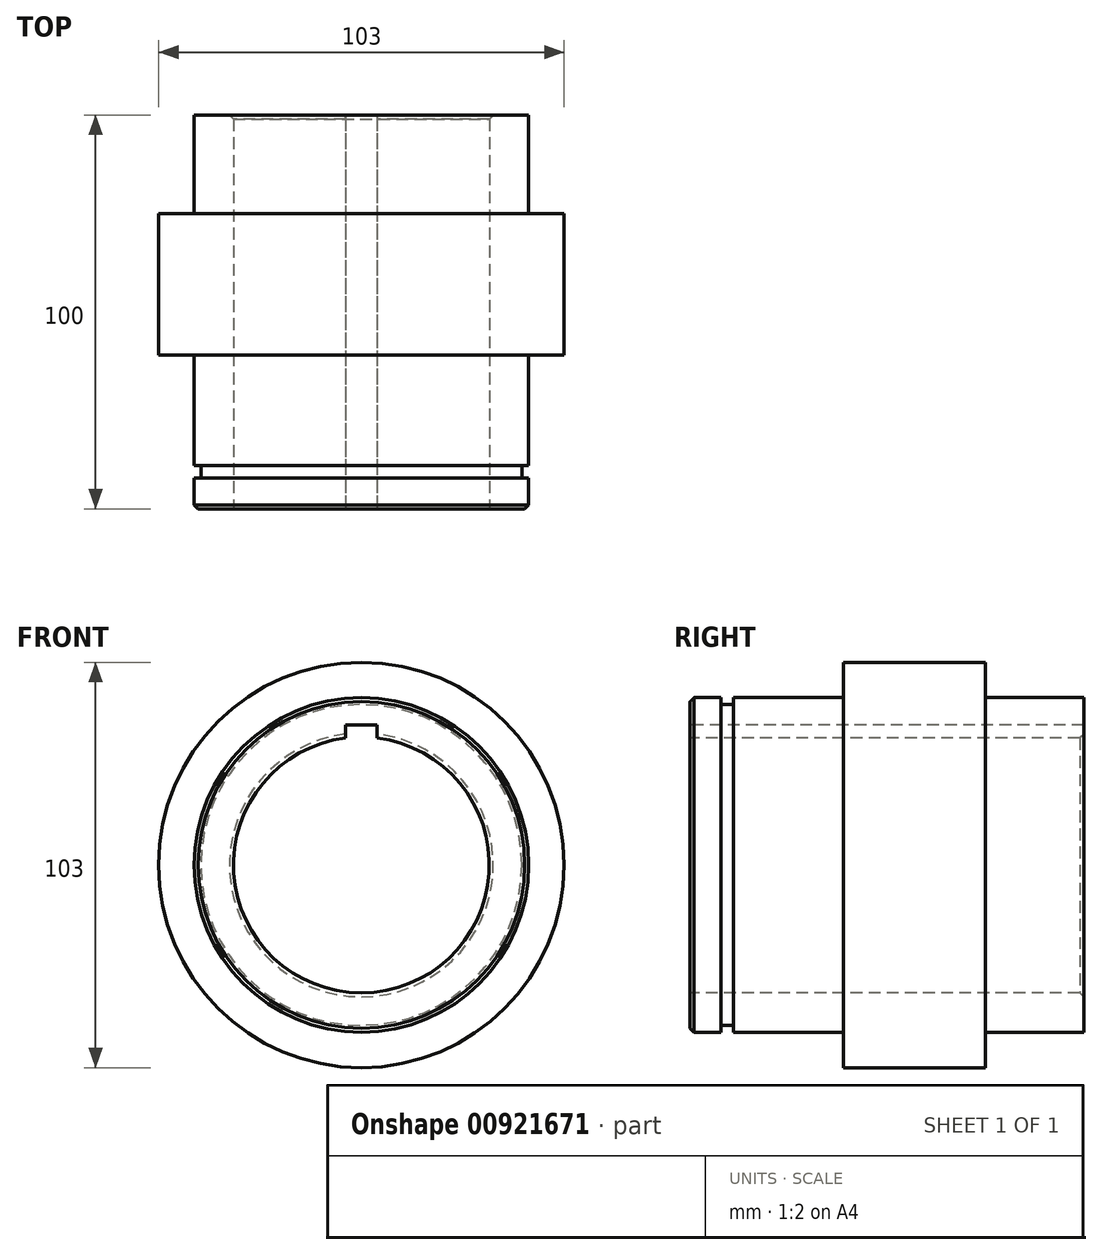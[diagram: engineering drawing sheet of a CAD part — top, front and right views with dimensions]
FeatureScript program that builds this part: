
annotation { "Feature Type Name" : "Feature", "Feature Type Description" : "" }
export const myFeature = defineFeature(function(context is Context, id is Id, definition is map)
    precondition{}
    {
        {
            var Q0;
            Q0=qCreatedBy(makeId("Right.planeOp"),FACE);
            var sketch = newSketch(context, id + "F0", { "sketchPlane" : qUnion([Q0])});
            skLineSegment(sketch, "E0", {"start": v(-132.05, 0) * mm, "end": v(300.03, 0) * mm, "construction": true});
            skLineSegment(sketch, "E1", {"start": v(-142.5, 0) * mm, "end": v(-142.5, 42.5) * mm});
            skLineSegment(sketch, "E2", {"start": v(-142.5, 42.5) * mm, "end": v(-134.65, 42.5) * mm});
            skLineSegment(sketch, "E3", {"start": v(-134.65, 42.5) * mm, "end": v(-134.65, 40.75) * mm});
            skLineSegment(sketch, "E4", {"start": v(-134.65, 40.75) * mm, "end": v(-131.5, 40.75) * mm});
            skLineSegment(sketch, "E5", {"start": v(-131.5, 40.75) * mm, "end": v(-131.5, 42.5) * mm});
            skLineSegment(sketch, "E6", {"start": v(-131.5, 42.5) * mm, "end": v(-103.5, 42.5) * mm});
            skLineSegment(sketch, "E7", {"start": v(-103.5, 42.5) * mm, "end": v(-103.5, 51.5) * mm});
            skLineSegment(sketch, "E8", {"start": v(-103.5, 51.5) * mm, "end": v(-67.5, 51.5) * mm});
            skLineSegment(sketch, "E9", {"start": v(-67.5, 51.5) * mm, "end": v(-67.5, 42.5) * mm});
            skLineSegment(sketch, "E10", {"start": v(-67.5, 42.5) * mm, "end": v(-42.5, 42.5) * mm});
            skLineSegment(sketch, "E11", {"start": v(-42.5, 42.5) * mm, "end": v(-42.5, 0) * mm});
            skLineSegment(sketch, "E12", {"start": v(-42.5, 0) * mm, "end": v(-142.5, 0) * mm});
            skSolve(sketch);
        }
        {
            var Q0;
            Q0=makeQuery(id+"F0.imprint","IMPRINT",FACE,{"disambiguationData":[TD([[makeQuery(id+"F0.imprint","IMPRINT",EDGE,{"derivedFrom":sQuery(id+"F0.wireOp",EDGE,"E1")}),-1.0]])]});
            var Q1;
            Q1=sQuery(id+"F0.wireOp",EDGE,"E12");
            revolve(context, id + "F1", {"surfaceOperationType" : NewSurfaceOperationType.NEW, "entities" : qUnion([Q0]), "axis" : qUnion([Q1]), "revolveType" : RevolveType.FULL});
        }
        {
            var Q0;
            Q0=makeQuery(id+"F1.opRevolve","SWEPT_FACE",FACE,{"disambiguationData":[OSD([sQuery(id+"F0.wireOp",EDGE,"E1")])]});
            var sketch = newSketch(context, id + "F2", { "sketchPlane" : qUnion([Q0])});
            skSolve(sketch);
        }
        {
            var Q0;
            Q0=makeQuery(id+"F2.imprint","IMPRINT",FACE,{"disambiguationData":[TD([[makeQuery(id+"F2.imprint","IMPRINT",EDGE,{"derivedFrom":makeQuery(id+"F1.opRevolve","SWEPT_EDGE",EDGE,{"disambiguationData":[OSD([sQuery(id+"F0.wireOp",EDGE,"E1"),sQuery(id+"F0.wireOp",EDGE,"E2")])]})}),-1.0]])]});
            var sketch = newSketch(context, id + "F3", { "sketchPlane" : qUnion([Q0])});
            skLineSegment(sketch, "E13", {"start": v(-95.88, 0) * mm, "end": v(119.38, 0) * mm, "construction": true});
            skLineSegment(sketch, "E14", {"start": v(0, 89.66) * mm, "end": v(0, -91.15) * mm, "construction": true});
            skArc(sketch, "E15", {"start": v(-4, 32.25) * mm, "mid": v(0, -32.5) * mm, "end": v(4, 32.25) * mm});
            skLineSegment(sketch, "E16", {"start": v(-4, 32.25) * mm, "end": v(-4, 35.55) * mm});
            skLineSegment(sketch, "E17", {"start": v(-4, 35.55) * mm, "end": v(4, 35.55) * mm});
            skLineSegment(sketch, "E18", {"start": v(4, 35.55) * mm, "end": v(4, 32.25) * mm});
            skSolve(sketch);
        }
        {
            var Q0;
            Q0=makeQuery(id+"F3.imprint","IMPRINT",FACE,{"disambiguationData":[TD([[makeQuery(id+"F3.imprint","IMPRINT",EDGE,{"derivedFrom":sQuery(id+"F3.wireOp",EDGE,"E15")}),1.0]])]});
            extrude(context, id + "F4", {"entities" : qUnion([Q0]), "operationType" : NewBodyOperationType.REMOVE, "endBound" : BoundingType.THROUGH_ALL, "oppositeDirection" : true, "depth" : 25 * mm, "offsetDistance" : 25 * mm});
        }
        {
            var Q0;
            Q0=makeQuery(id+"F1.opRevolve","SWEPT_EDGE",EDGE,{"disambiguationData":[OSD([sQuery(id+"F0.wireOp",EDGE,"E1"),sQuery(id+"F0.wireOp",EDGE,"E2")])]});
            var Q1;
            Q1=makeQuery(id+"F4.boolean.opBoolean","INTERSECT",EDGE,{"derivedFrom":[makeQuery(id+"F1.opRevolve","SWEPT_FACE",FACE,{"disambiguationData":[OSD([sQuery(id+"F0.wireOp",EDGE,"E11")])]}),makeQuery(id+"F4.opExtrude","SWEPT_FACE",FACE,{"disambiguationData":[OSD([sQuery(id+"F3.wireOp",EDGE,"E15")])]})]});
            chamfer(context, id + "F5", {"entities" : qUnion([Q0, Q1]), "width" : 1 * mm, "tangentPropagation" : true});
        }
    });
